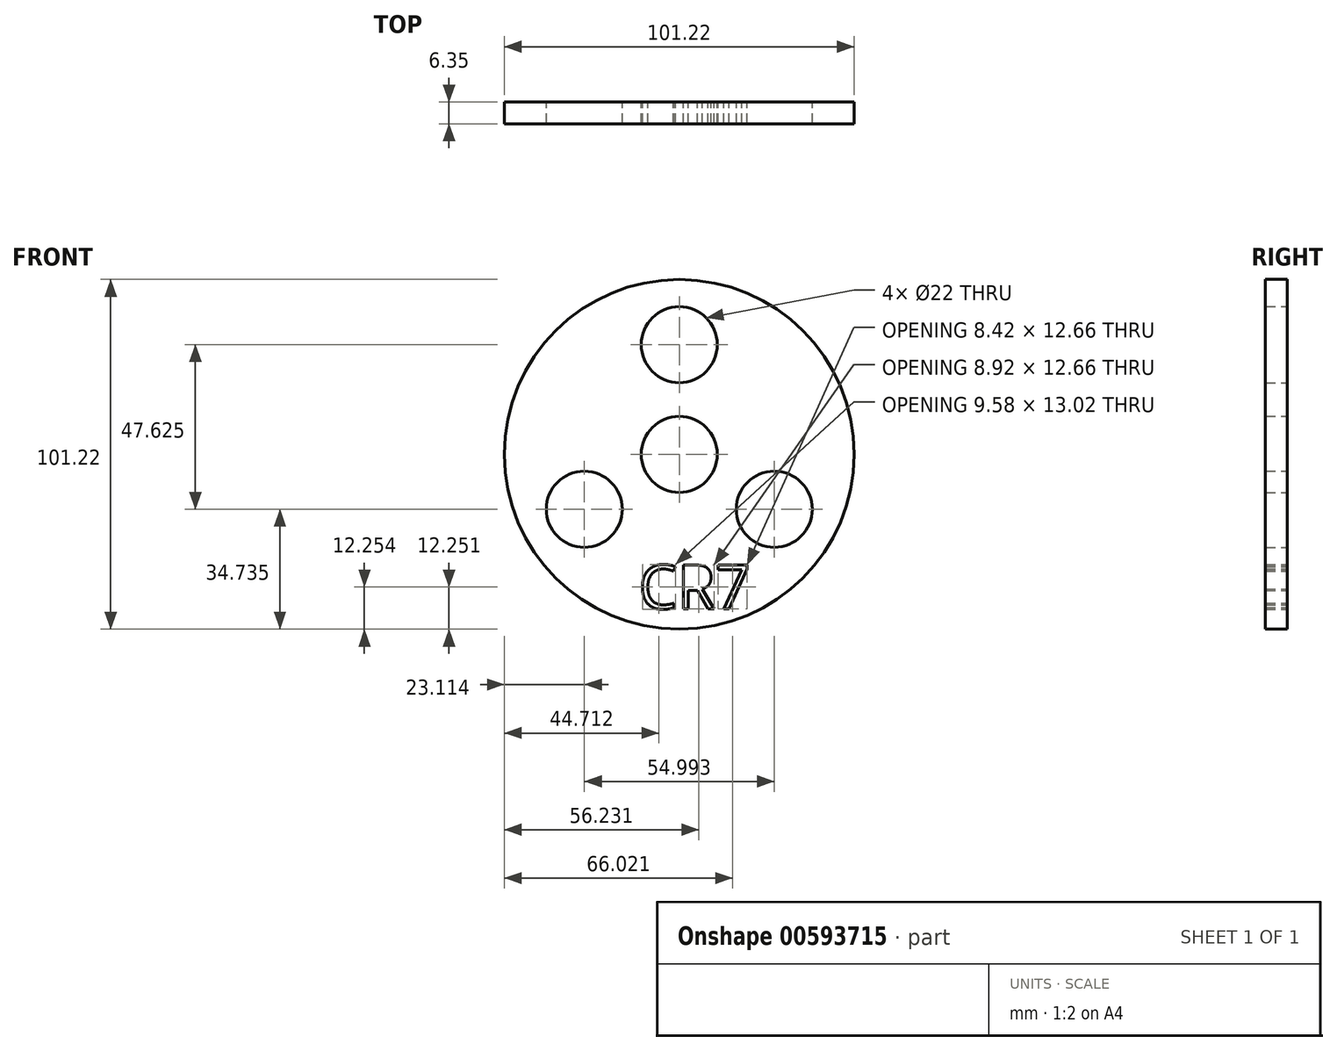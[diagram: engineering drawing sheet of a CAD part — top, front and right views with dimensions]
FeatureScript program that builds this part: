
annotation { "Feature Type Name" : "Feature", "Feature Type Description" : "" }
export const myFeature = defineFeature(function(context is Context, id is Id, definition is map)
    precondition{}
    {
        {
            var Q0;
            Q0=qCreatedBy(makeId("Front.planeOp"),FACE);
            var sketch = newSketch(context, id + "F0", { "sketchPlane" : qUnion([Q0])});
            skCircle(sketch, "E0", {"center": v(0, 31.75) * mm, "radius": 14.29 * mm});
            skCircle(sketch, "E1", {"center": v(0, 0) * mm, "radius": 14.29 * mm});
            skCircle(sketch, "E2", {"center": v(0, 31.75) * mm, "radius": 11 * mm});
            skCircle(sketch, "E3", {"center": v(0, 0) * mm, "radius": 11 * mm});
            skCircle(sketch, "E4.1.0", {"center": v(-27.5, -15.87) * mm, "radius": 14.29 * mm});
            skCircle(sketch, "E4.2.0", {"center": v(27.5, -15.88) * mm, "radius": 14.29 * mm});
            skCircle(sketch, "E5", {"center": v(-27.5, -15.87) * mm, "radius": 11 * mm});
            skCircle(sketch, "E6", {"center": v(27.5, -15.88) * mm, "radius": 11 * mm});
            skSolve(sketch);
        }
        {
            var Q0;
            Q0=qCreatedBy(makeId("Front.planeOp"),FACE);
            var sketch = newSketch(context, id + "F1", { "sketchPlane" : qUnion([Q0])});
            skCircle(sketch, "E7", {"center": v(0, 0) * mm, "radius": 50.6 * mm});
            skText(sketch, "E8", { "text": "CR7\n", "fontName": "OpenSans-Regular.ttf"});
            const initialGuessF1  = {"E8": [-0.01177, -0.04469, 1, 0, 0.01277]};
            skSetInitialGuess(sketch, initialGuessF1);
            skSolve(sketch);
        }
        {
            var Q0;
            Q0 = qSketchRegion(id + "F1", true);
            extrude(context, id + "F2", {"entities" : qUnion([Q0]), "depth" : 6.35 * mm, "offsetDistance" : 25.4 * mm});
        }
        {
            var Q0;
            Q0=makeQuery(id+"F0.imprint","IMPRINT",FACE,{"disambiguationData":[TD([[makeQuery(id+"F0.imprint","IMPRINT",EDGE,{"derivedFrom":sQuery(id+"F0.wireOp",EDGE,"E2")}),1.0]])]});
            var Q1;
            Q1=makeQuery(id+"F0.imprint","IMPRINT",FACE,{"disambiguationData":[TD([[makeQuery(id+"F0.imprint","IMPRINT",EDGE,{"derivedFrom":sQuery(id+"F0.wireOp",EDGE,"E3")}),1.0]])]});
            var Q2;
            Q2=makeQuery(id+"F0.imprint","IMPRINT",FACE,{"disambiguationData":[TD([[makeQuery(id+"F0.imprint","IMPRINT",EDGE,{"derivedFrom":sQuery(id+"F0.wireOp",EDGE,"E5")}),1.0]])]});
            var Q3;
            Q3=makeQuery(id+"F0.imprint","IMPRINT",FACE,{"disambiguationData":[TD([[makeQuery(id+"F0.imprint","IMPRINT",EDGE,{"derivedFrom":sQuery(id+"F0.wireOp",EDGE,"E6")}),1.0]])]});
            extrude(context, id + "F3", {"entities" : qUnion([Q0, Q1, Q2, Q3]), "operationType" : NewBodyOperationType.REMOVE, "depth" : 6.35 * mm, "offsetDistance" : 25.4 * mm});
        }
    });
